# Revit family: 2020.08.13
name_source: partatom
category: Устройства связи
revit_build: Autodesk Revit 2018 (Build: 20181011_1500(x64)
units: mm (PartAtom-declared; Revit-internal decimal feet)

## family parameters
Общий = Нет
Основа = Грань
При загрузке вырезать с полостями = Нет
Размер круглого соединителя = Использовать диаметр
Сохранять ориентацию аннотаций = Да
Тип детали = Нормальный
Точка расчета площади = Нет

## types (3) — shared parameters
ADSK_Версия Revit = 2018
ADSK_Версия семейства = v2
ADSK_Единица измерения = шт.
ADSK_Завод-изготовитель = ООО «Видеомакс»
ADSK_Код изделия = ТУ 26.20.15-003-37165186-2020
ADSK_Количество = 1
ADSK_Коэффициент мощности = 0.96
ADSK_Марка = VIDEOMAX-URM
ADSK_Напряжение = 230 В
ADSK_Номинальная мощность = 0 В·А
ADSK_Ток = 0 А
Material = Черный
URL = https://www.videomax-server.ru
Изготовитель = ООО «Видеомакс»
Количество входов 230V, шт = 1
Количество интерфейсов Gigabit LAN, шт = 1
Максимальное количество подключаемых мониторов, шт = 1
Отметка по умолчанию = 2600 мм
Указания по монтажу = Для настольного размещения. Специальные монтажные аксессуары не требуются.
zero-valued in all types: ADSK_Масса, Количество интерфейсов 10 Gigabit LAN, шт, Максимальная мощность БП, Вт, Максимальная потребляемая мощность Вт, Максимальное тепловыделение, BTU/h, Стоимость

## per-type parameters (varying)
| type | ADSK_Наименование | Back | Front | ITX | Left | MIDI TOWER | MINI TOWER | Right | Высота | Глубина | Изображение типоразмера | Ширина |
| ITX | УРМ настольного исполнения ITX | videomax_itx : Back | videomax_itx : Front | Да | videomax_itx : Left | Нет | Нет | videomax_itx : Right | 63 мм | 220 мм | Micro ITX.png | 197 мм |
| MINI TOWER | УРМ настольного исполнения MINI TOWER | videomax_minitower : Back | videomax_minitower : Front | Нет | videomax_minitower : Left | Нет | Да | videomax_minitower : Right | 325 мм | 425 мм | Mini Tower.png | 180 мм |
| MIDI TOWER | УРМ настольного исполнения MIDI TOWER | videomax_miditower : Back | videomax_miditower : Front | Нет | videomax_miditower : Left | Да | Нет | videomax_miditower : Right | 410 мм | 428 мм | Midi Tower.png | 160 мм |

note: column(s) folded — value = type name in every type: ADSK_Обозначение
